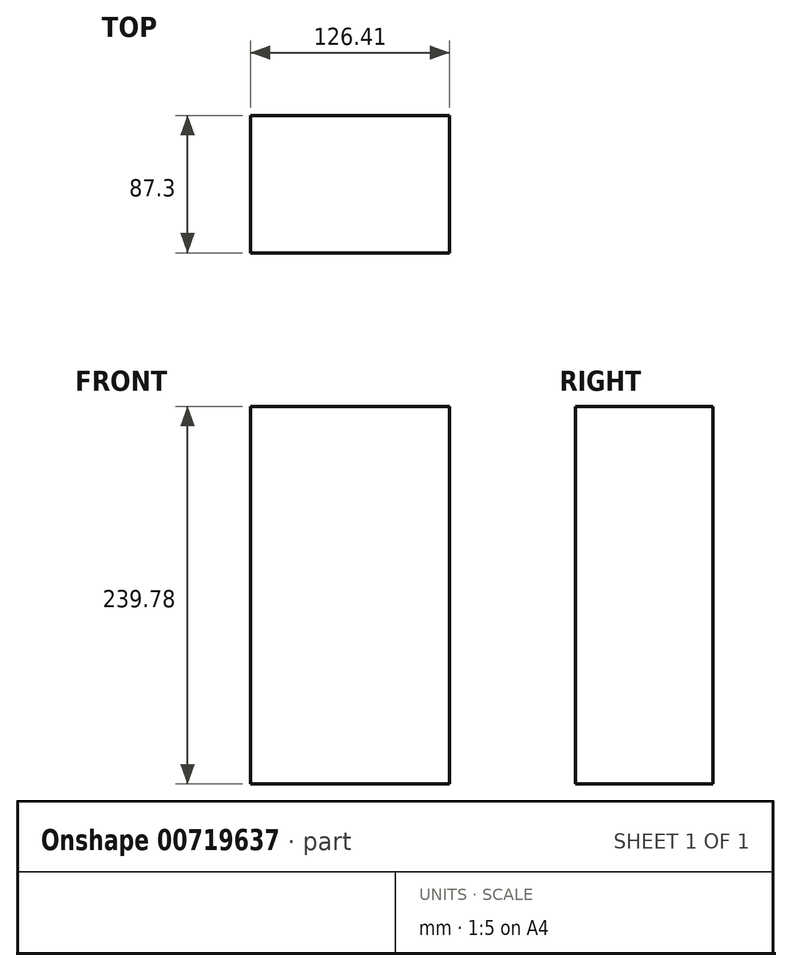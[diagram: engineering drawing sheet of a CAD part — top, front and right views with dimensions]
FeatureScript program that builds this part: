
annotation { "Feature Type Name" : "Feature", "Feature Type Description" : "" }
export const myFeature = defineFeature(function(context is Context, id is Id, definition is map)
    precondition{}
    {
        {
            var Q0;
            Q0=qCreatedBy(makeId("Top.planeOp"),FACE);
            var sketch = newSketch(context, id + "F0", { "sketchPlane" : qUnion([Q0])});
            skLineSegment(sketch, "E0.bottom", {"start": v(-65.86, 42.9) * mm, "end": v(60.55, 42.9) * mm});
            skLineSegment(sketch, "E0.top", {"start": v(-65.86, -44.41) * mm, "end": v(60.55, -44.41) * mm});
            skLineSegment(sketch, "E0.left", {"start": v(-65.86, 42.9) * mm, "end": v(-65.86, -44.41) * mm});
            skLineSegment(sketch, "E0.right", {"start": v(60.55, 42.9) * mm, "end": v(60.55, -44.41) * mm});
            skSolve(sketch);
        }
        {
            var Q0;
            Q0=makeQuery(id+"F0.imprint","IMPRINT",FACE,{"disambiguationData":[TD([[makeQuery(id+"F0.imprint","IMPRINT",EDGE,{"derivedFrom":sQuery(id+"F0.wireOp",EDGE,"E0.bottom")}),-1.0]])]});
            extrude(context, id + "F1", {"entities" : qUnion([Q0]), "endBound" : BoundingType.SYMMETRIC, "depth" : 239.78 * mm, "offsetDistance" : 25.4 * mm});
        }
    });
